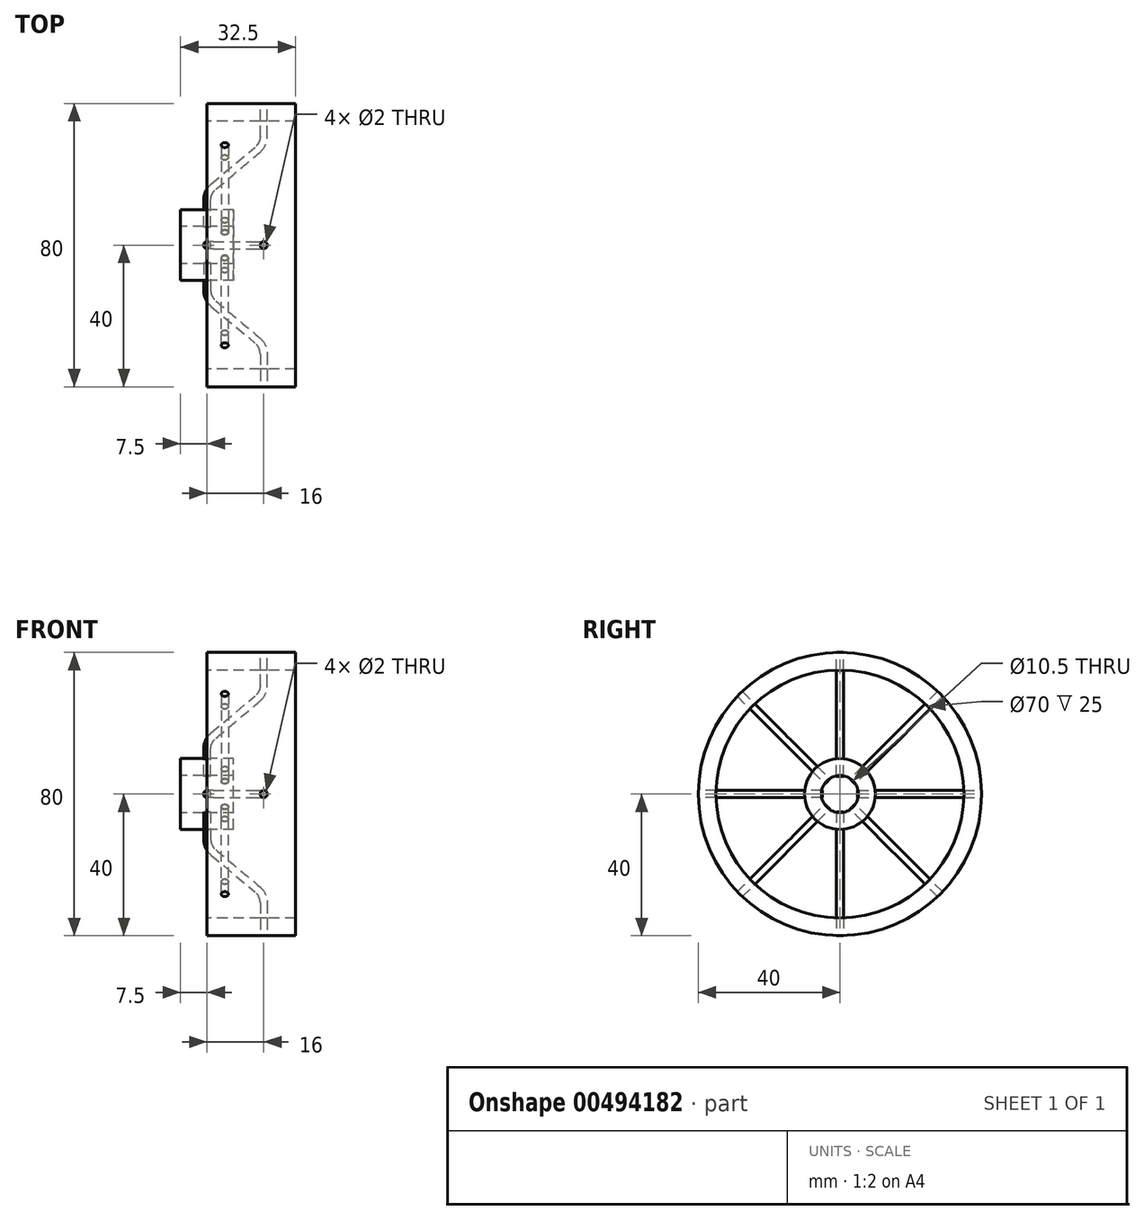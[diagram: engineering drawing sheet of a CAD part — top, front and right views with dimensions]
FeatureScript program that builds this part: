
annotation { "Feature Type Name" : "Feature", "Feature Type Description" : "" }
export const myFeature = defineFeature(function(context is Context, id is Id, definition is map)
    precondition{}
    {
        {
            var Q0;
            Q0=qCreatedBy(makeId("Right.planeOp"),FACE);
            var sketch = newSketch(context, id + "F0", { "sketchPlane" : qUnion([Q0])});
            skCircle(sketch, "E0", {"center": v(0, 0) * mm, "radius": 5.25 * mm});
            skCircle(sketch, "E1", {"center": v(0, 0) * mm, "radius": 10 * mm});
            skCircle(sketch, "E2", {"center": v(0, 0) * mm, "radius": 35 * mm});
            skCircle(sketch, "E3", {"center": v(0, 0) * mm, "radius": 40 * mm});
            skSolve(sketch);
        }
        {
            var Q0;
            Q0=qCreatedBy(makeId("Front.planeOp"),FACE);
            var sketch = newSketch(context, id + "F1", { "sketchPlane" : qUnion([Q0])});
            skLineSegment(sketch, "E4", {"start": v(0, 5) * mm, "end": v(0, 12.67) * mm});
            skLineSegment(sketch, "E5", {"start": v(1.79, 16.5) * mm, "end": v(14.21, 26.93) * mm});
            skLineSegment(sketch, "E6", {"start": v(16, 30.76) * mm, "end": v(16, 40) * mm});
            skPoint(sketch, "E7.visualSharp", {"position": v(16, 28.43) * mm});
            skArc(sketch, "E7.filletArc", {"start": v(14.21, 26.93) * mm, "mid": v(15.53, 28.64) * mm, "end": v(16, 30.76) * mm});
            skPoint(sketch, "E8.visualSharp", {"position": v(0, 15) * mm});
            skArc(sketch, "E8.filletArc", {"start": v(1.79, 16.5) * mm, "mid": v(0.47, 14.78) * mm, "end": v(0, 12.67) * mm});
            skSolve(sketch);
        }
        {
            var Q0;
            Q0=qCreatedBy(makeId("Top.planeOp"),FACE);
            var Q1;
            Q1=sQuery(id+"F1.wireOp",VERTEX,"E4.start");
            cPlane(context, id + "F2", {"entities" : qUnion([Q0, Q1]), "cplaneType" : CPlaneType.PLANE_POINT, "offset" : 25 * mm, "width" : 150 * mm, "height" : 150 * mm});
        }
        {
            var Q0;
            Q0=qCreatedBy(id+"F2.planeOp",FACE);
            var sketch = newSketch(context, id + "F3", { "sketchPlane" : qUnion([Q0])});
            skCircle(sketch, "E9", {"center": v(0, 0) * mm, "radius": 1 * mm});
            skSolve(sketch);
        }
        {
            var Q0;
            Q0=makeQuery(id+"F3.imprint","IMPRINT",FACE,{"disambiguationData":[TD([[makeQuery(id+"F3.imprint","IMPRINT",EDGE,{"derivedFrom":sQuery(id+"F3.wireOp",EDGE,"E9")}),1.0]])]});
            var Q1;
            Q1=sQuery(id+"F1.wireOp",EDGE,"E4");
            var Q2;
            Q2=sQuery(id+"F1.wireOp",EDGE,"E8.filletArc");
            var Q3;
            Q3=sQuery(id+"F1.wireOp",EDGE,"E5");
            var Q4;
            Q4=sQuery(id+"F1.wireOp",EDGE,"E7.filletArc");
            var Q5;
            Q5=sQuery(id+"F1.wireOp",EDGE,"E6");
            sweep(context, id + "F4", {"profiles" : qUnion([Q0]), "path" : qUnion([Q1, Q2, Q3, Q4, Q5])});
        }
        {
            var Q0;
            Q0=makeQuery(id+"F0.imprint","IMPRINT",FACE,{"disambiguationData":[TD([[makeQuery(id+"F0.imprint","IMPRINT",EDGE,{"derivedFrom":sQuery(id+"F0.wireOp",EDGE,"E0")}),-1.0]])]});
            extrude(context, id + "F5", {"entities" : qUnion([Q0]), "endBound" : BoundingType.SYMMETRIC, "depth" : 15 * mm});
        }
        {
            var Q0;
            Q0=makeQuery(id+"F0.imprint","IMPRINT",FACE,{"disambiguationData":[TD([[makeQuery(id+"F0.imprint","IMPRINT",EDGE,{"derivedFrom":sQuery(id+"F0.wireOp",EDGE,"E2")}),-1.0]])]});
            extrude(context, id + "F6", {"entities" : qUnion([Q0]), "depth" : 25 * mm});
        }
        {
            var Q0;
            Q0=makeQuery(id+"F4.opSweep","SWEPT_BODY",BODY,{"disambiguationData":[OSD([sQuery(id+"F1.wireOp",EDGE,"E6"),sQuery(id+"F3.wireOp",EDGE,"E9")])]});
            var Q1;
            Q1=sQuery(id+"F0.wireOp",EDGE,"E0");
            circularPattern(context, id + "F7", {"entities" : qUnion([Q0]), "axis" : qUnion([Q1]), "angle" : 360 * degree, "instanceCount" : 4, "equalSpace" : true});
        }
        {
            var Q0;
            Q0=makeQuery(id+"F7.opPattern","COPY",BODY,{"derivedFrom":makeQuery(id+"F4.opSweep","SWEPT_BODY",BODY,{"disambiguationData":[OSD([sQuery(id+"F1.wireOp",EDGE,"E6"),sQuery(id+"F3.wireOp",EDGE,"E9")])]}),"instanceName":"5"});
            var Q1;
            Q1=makeQuery(id+"F4.opSweep","SWEPT_BODY",BODY,{"disambiguationData":[OSD([sQuery(id+"F1.wireOp",EDGE,"E6"),sQuery(id+"F3.wireOp",EDGE,"E9")])]});
            var Q2;
            Q2=makeQuery(id+"F7.opPattern","COPY",BODY,{"derivedFrom":makeQuery(id+"F4.opSweep","SWEPT_BODY",BODY,{"disambiguationData":[OSD([sQuery(id+"F1.wireOp",EDGE,"E6"),sQuery(id+"F3.wireOp",EDGE,"E9")])]}),"instanceName":"1"});
            var Q3;
            Q3=makeQuery(id+"F7.opPattern","COPY",BODY,{"derivedFrom":makeQuery(id+"F4.opSweep","SWEPT_BODY",BODY,{"disambiguationData":[OSD([sQuery(id+"F1.wireOp",EDGE,"E6"),sQuery(id+"F3.wireOp",EDGE,"E9")])]}),"instanceName":"2"});
            var Q4;
            Q4=makeQuery(id+"F7.opPattern","COPY",BODY,{"derivedFrom":makeQuery(id+"F4.opSweep","SWEPT_BODY",BODY,{"disambiguationData":[OSD([sQuery(id+"F1.wireOp",EDGE,"E6"),sQuery(id+"F3.wireOp",EDGE,"E9")])]}),"instanceName":"3"});
            var Q5;
            Q5=makeQuery(id+"F7.opPattern","COPY",BODY,{"derivedFrom":makeQuery(id+"F4.opSweep","SWEPT_BODY",BODY,{"disambiguationData":[OSD([sQuery(id+"F1.wireOp",EDGE,"E6"),sQuery(id+"F3.wireOp",EDGE,"E9")])]}),"instanceName":"4"});
            var Q6;
            Q6=makeQuery(id+"F6.opExtrude","SWEPT_BODY",BODY,{"disambiguationData":[OSD([sQuery(id+"F0.wireOp",EDGE,"E2"),sQuery(id+"F0.wireOp",EDGE,"E3")])]});
            var Q7;
            Q7=makeQuery(id+"F5.opExtrude","SWEPT_BODY",BODY,{"disambiguationData":[OSD([sQuery(id+"F0.wireOp",EDGE,"E0"),sQuery(id+"F0.wireOp",EDGE,"E1")])]});
            booleanBodies(context, id + "F8", {"operationType" : BooleanOperationType.SUBTRACTION, "tools" : qUnion([Q0, Q1, Q2, Q3, Q4, Q5]), "targets" : qUnion([Q6, Q7]), "keepTools" : true});
        }
        {
            var Q0;
            Q0=makeQuery(id+"F5.opExtrude","SWEPT_FACE",FACE,{"disambiguationData":[OSD([sQuery(id+"F0.wireOp",EDGE,"E0")])]});
            cPlane(context, id + "F9", {"entities" : qUnion([Q0]), "cplaneType" : CPlaneType.LINE_ANGLE, "offset" : 25 * mm, "angle" : 45 * degree, "width" : 150 * mm, "height" : 150 * mm});
        }
        {
            var Q0;
            Q0=qCreatedBy(id+"F9.planeOp",FACE);
            cPlane(context, id + "F10", {"entities" : qUnion([Q0]), "cplaneType" : CPlaneType.OFFSET, "offset" : 5 * mm, "width" : 150 * mm, "height" : 150 * mm});
        }
        {
            var Q0;
            Q0=qCreatedBy(id+"F10.planeOp",FACE);
            var sketch = newSketch(context, id + "F11", { "sketchPlane" : qUnion([Q0])});
            skCircle(sketch, "E10", {"center": v(-5, 0) * mm, "radius": 1 * mm});
            skSolve(sketch);
        }
        {
            var Q0;
            Q0=makeQuery(id+"F11.imprint","IMPRINT",FACE,{"disambiguationData":[TD([[makeQuery(id+"F11.imprint","IMPRINT",EDGE,{"derivedFrom":sQuery(id+"F11.wireOp",EDGE,"E10")}),1.0]])]});
            var Q1;
            Q1=makeQuery(id+"F6.opExtrude","SWEPT_FACE",FACE,{"disambiguationData":[OSD([sQuery(id+"F0.wireOp",EDGE,"E3")])]});
            extrude(context, id + "F12", {"entities" : qUnion([Q0]), "endBound" : BoundingType.UP_TO_SURFACE, "endBoundEntityFace" : qUnion([Q1]), "depth" : 25 * mm});
        }
        {
            var Q0;
            Q0=makeQuery(id+"F12.opExtrude","SWEPT_BODY",BODY,{"disambiguationData":[OSD([sQuery(id+"F11.wireOp",EDGE,"E10")])]});
            var Q1;
            Q1=makeQuery(id+"F5.opExtrude","CAP_EDGE",EDGE,{"disambiguationData":[OSD([sQuery(id+"F0.wireOp",EDGE,"E0")])],"isStart":true});
            circularPattern(context, id + "F13", {"entities" : qUnion([Q0]), "axis" : qUnion([Q1]), "angle" : 360 * degree, "instanceCount" : 4, "equalSpace" : true});
        }
        {
            var Q0;
            Q0=makeQuery(id+"F13.opPattern","COPY",BODY,{"derivedFrom":makeQuery(id+"F12.opExtrude","SWEPT_BODY",BODY,{"disambiguationData":[OSD([sQuery(id+"F11.wireOp",EDGE,"E10")])]}),"instanceName":"3"});
            var Q1;
            Q1=makeQuery(id+"F12.opExtrude","SWEPT_BODY",BODY,{"disambiguationData":[OSD([sQuery(id+"F11.wireOp",EDGE,"E10")])]});
            var Q2;
            Q2=makeQuery(id+"F13.opPattern","COPY",BODY,{"derivedFrom":makeQuery(id+"F12.opExtrude","SWEPT_BODY",BODY,{"disambiguationData":[OSD([sQuery(id+"F11.wireOp",EDGE,"E10")])]}),"instanceName":"1"});
            var Q3;
            Q3=makeQuery(id+"F13.opPattern","COPY",BODY,{"derivedFrom":makeQuery(id+"F12.opExtrude","SWEPT_BODY",BODY,{"disambiguationData":[OSD([sQuery(id+"F11.wireOp",EDGE,"E10")])]}),"instanceName":"2"});
            var Q4;
            Q4=makeQuery(id+"F6.opExtrude","SWEPT_BODY",BODY,{"disambiguationData":[OSD([sQuery(id+"F0.wireOp",EDGE,"E2"),sQuery(id+"F0.wireOp",EDGE,"E3")])]});
            var Q5;
            Q5=makeQuery(id+"F5.opExtrude","SWEPT_BODY",BODY,{"disambiguationData":[OSD([sQuery(id+"F0.wireOp",EDGE,"E0"),sQuery(id+"F0.wireOp",EDGE,"E1")])]});
            booleanBodies(context, id + "F14", {"operationType" : BooleanOperationType.SUBTRACTION, "tools" : qUnion([Q0, Q1, Q2, Q3]), "targets" : qUnion([Q4, Q5]), "keepTools" : true});
        }
    });
